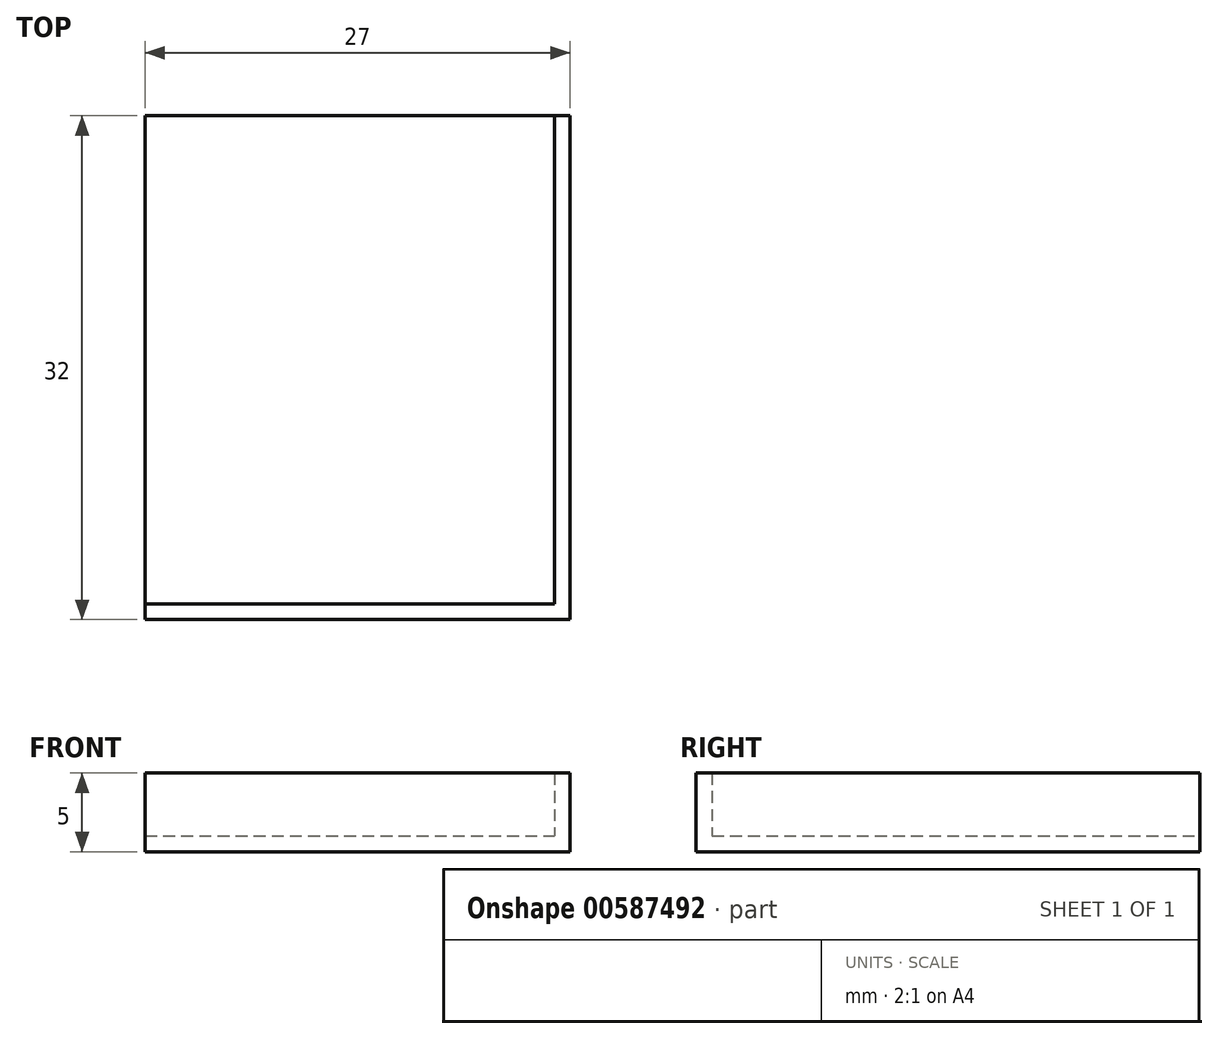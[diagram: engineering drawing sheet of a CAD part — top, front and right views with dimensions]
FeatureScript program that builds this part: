
annotation { "Feature Type Name" : "Feature", "Feature Type Description" : "" }
export const myFeature = defineFeature(function(context is Context, id is Id, definition is map)
    precondition{}
    {
        {
            var Q0;
            Q0=qCreatedBy(makeId("Top.planeOp"),FACE);
            var sketch = newSketch(context, id + "F0", { "sketchPlane" : qUnion([Q0])});
            skLineSegment(sketch, "E0.bottom", {"start": v(0, 0) * mm, "end": v(27, 0) * mm});
            skLineSegment(sketch, "E0.top", {"start": v(0, 32) * mm, "end": v(27, 32) * mm});
            skLineSegment(sketch, "E0.left", {"start": v(0, 0) * mm, "end": v(0, 32) * mm});
            skLineSegment(sketch, "E0.right", {"start": v(27, 0) * mm, "end": v(27, 32) * mm});
            skSolve(sketch);
        }
        {
            var Q0;
            Q0 = qSketchRegion(id + "F0", true);
            extrude(context, id + "F1", {"entities" : qUnion([Q0]), "depth" : 1 * mm, "offsetDistance" : 25 * mm});
        }
        {
            var Q0;
            Q0=makeQuery(id+"F1.opExtrude","CAP_FACE",FACE,{"disambiguationData":[OSD([sQuery(id+"F0.wireOp",EDGE,"E0.bottom"),sQuery(id+"F0.wireOp",EDGE,"E0.top"),sQuery(id+"F0.wireOp",EDGE,"E0.left"),sQuery(id+"F0.wireOp",EDGE,"E0.right")])],"isStart":false});
            var sketch = newSketch(context, id + "F2", { "sketchPlane" : qUnion([Q0])});
            skLineSegment(sketch, "E1.0", {"start": v(0, 1) * mm, "end": v(26, 1) * mm});
            skLineSegment(sketch, "E2.0", {"start": v(26, 1) * mm, "end": v(26, 32) * mm});
            skLineSegment(sketch, "E3", {"start": v(0, 1) * mm, "end": v(0, 0) * mm});
            skLineSegment(sketch, "E4", {"start": v(0, 0) * mm, "end": v(27, 0) * mm});
            skLineSegment(sketch, "E5", {"start": v(27, 0) * mm, "end": v(27, 32) * mm});
            skLineSegment(sketch, "E6", {"start": v(27, 32) * mm, "end": v(26, 32) * mm});
            skSolve(sketch);
        }
        {
            var Q0;
            Q0 = qSketchRegion(id + "F2", true);
            extrude(context, id + "F3", {"entities" : qUnion([Q0]), "operationType" : NewBodyOperationType.ADD, "depth" : 4 * mm, "offsetDistance" : 25 * mm});
        }
    });
